# Revit family: Fan_Coil-Valveless-Whalen-Vertical_Stacked-Face_And_Bypass-2P-Electric_Heat
name_source: partatom
category: Mechanical Equipment
revit_build: Autodesk Revit MEP 2012 (Build: 20110916_2132(x64)
units: mm (PartAtom-declared; Revit-internal decimal feet)

## types (7) — shared parameters
Date Last Modified = 1/22/2014
Equipment Abbreviation = RFC
Family Version = 1.0.0
Frequency = 60 Hz
Load Classification = HVAC
Manufacturer = The Whalen Company
Model Disclaimer = Contact The Whalen Company for More Information
Product Documentation Link = http://www.whalencompany.com
Product Material = Steel - Whalen - Galvanized
Provide Feedback = https://www.surveymonkey.com
URL = http://www.whalencompany.com

## per-type parameters (varying)
| type | Actual Return Air Flow | Actual Supply Air Flow | Description | Model | Weight | zz Integer 3 |
| 200 CFM | 222 CFM | 222 CFM | Riser Heat-Exchanger Vertical Fan-Coil Units, 2 Pipe with Face and Bypass Damper Control, With Electric Heat, 200 CFM | W200 | 145.000 lb | 200 |
| 300 CFM | 241 CFM | 241 CFM | Riser Heat-Exchanger Vertical Fan-Coil Units, 2 Pipe with Face and Bypass Damper Control, With Electric Heat, 300 CFM | W300 | 145.000 lb | 300 |
| 300 CFM, Extended | 241 CFM | 241 CFM | Riser Heat-Exchanger Vertical Fan-Coil Units, 2 Pipe with Face and Bypass Damper Control, With Electric Heat, 300 CFM | W300X | 175.000 lb | 301 |
| 400 CFM | 362 CFM | 362 CFM | Riser Heat-Exchanger Vertical Fan-Coil Units, 2 Pipe with Face and Bypass Damper Control, With Electric Heat, 400 CFM | W400 | 180.000 lb | 400 |
| 500 CFM | 455 CFM | 455 CFM | Riser Heat-Exchanger Vertical Fan-Coil Units, 2 Pipe with Face and Bypass Damper Control, With Electric Heat, 500 CFM | W500 | 180.000 lb | 500 |
| 600 CFM | 580 CFM | 580 CFM | Riser Heat-Exchanger Vertical Fan-Coil Units, 2 Pipe with Face and Bypass Damper Control, With Electric Heat, 600 CFM | W600 | 210.000 lb | 600 |
| 800 CFM | 683 CFM | 683 CFM | Riser Heat-Exchanger Vertical Fan-Coil Units, 2 Pipe with Face and Bypass Damper Control, With Electric Heat, 800 CFM | W800 | 210.000 lb | 800 |

## geometry (parser evidence)
native form markers: Sweep x5
no freeform markers — native parametric forms only
